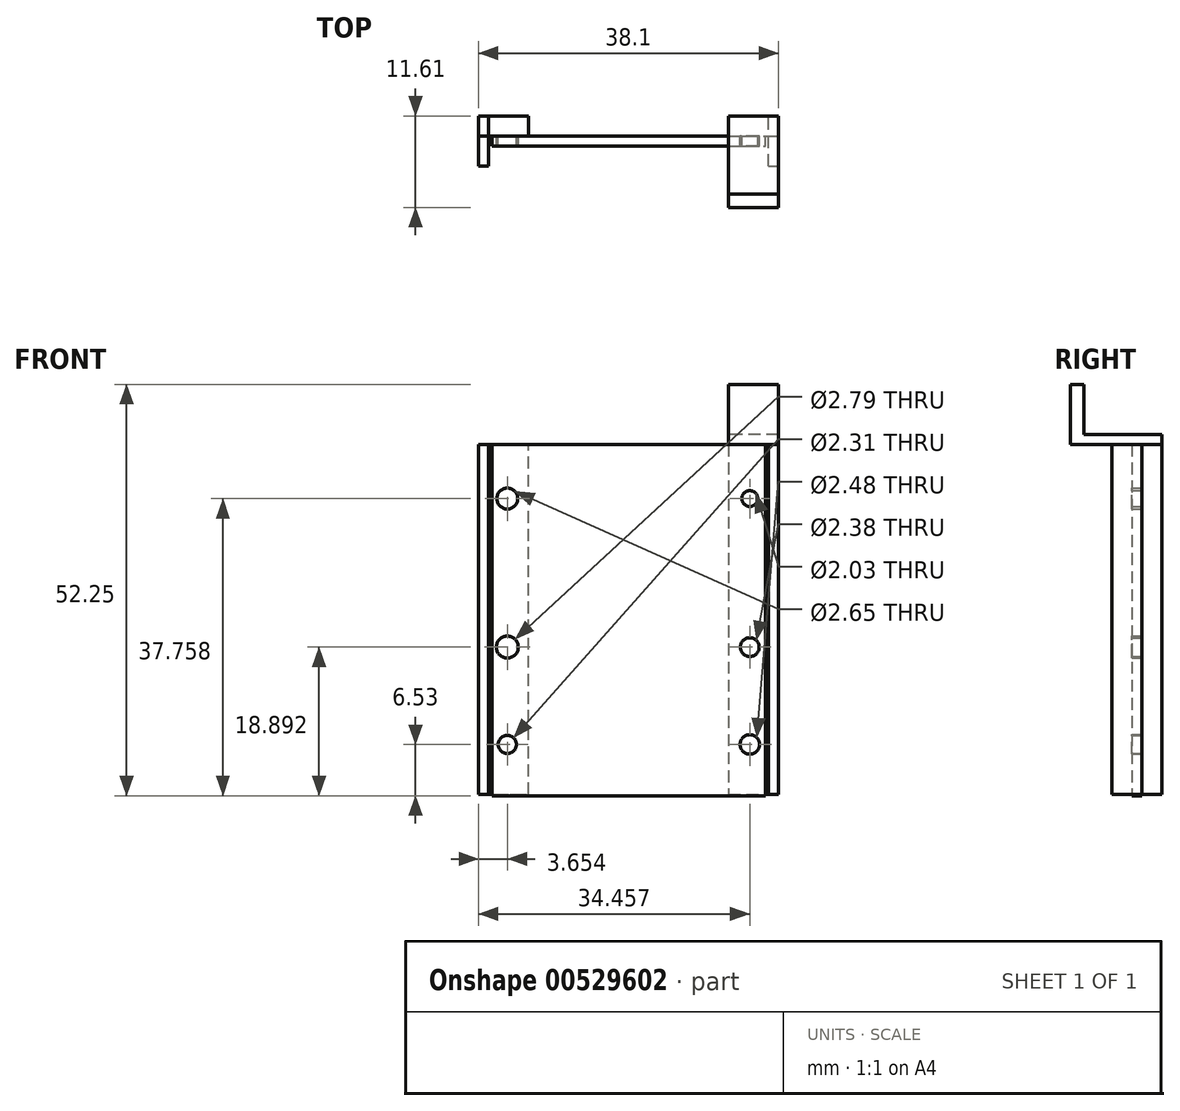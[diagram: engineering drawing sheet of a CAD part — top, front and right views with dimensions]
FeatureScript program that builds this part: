
annotation { "Feature Type Name" : "Feature", "Feature Type Description" : "" }
export const myFeature = defineFeature(function(context is Context, id is Id, definition is map)
    precondition{}
    {
        {
            var Q0;
            Q0=qCreatedBy(makeId("Front.planeOp"),FACE);
            var sketch = newSketch(context, id + "F0", { "sketchPlane" : qUnion([Q0])});
            skLineSegment(sketch, "E0.bottom", {"start": v(-19.05, -6.35) * mm, "end": v(-12.7, -6.35) * mm});
            skLineSegment(sketch, "E0.top", {"start": v(-19.05, 38.1) * mm, "end": v(-12.7, 38.1) * mm});
            skLineSegment(sketch, "E0.left", {"start": v(-19.05, -6.35) * mm, "end": v(-19.05, 38.1) * mm});
            skLineSegment(sketch, "E0.right", {"start": v(-12.7, -6.35) * mm, "end": v(-12.7, 38.1) * mm});
            skLineSegment(sketch, "E1.bottom", {"start": v(12.7, 38.1) * mm, "end": v(19.05, 38.1) * mm});
            skLineSegment(sketch, "E1.top", {"start": v(12.7, -6.35) * mm, "end": v(19.05, -6.35) * mm});
            skLineSegment(sketch, "E1.left", {"start": v(12.7, 38.1) * mm, "end": v(12.7, -6.35) * mm});
            skLineSegment(sketch, "E1.right", {"start": v(19.05, 38.1) * mm, "end": v(19.05, -6.35) * mm});
            skLineSegment(sketch, "E2", {"start": v(-17.78, -6.35) * mm, "end": v(-17.78, 38.1) * mm});
            skLineSegment(sketch, "E3", {"start": v(17.78, -6.35) * mm, "end": v(17.78, 38.1) * mm});
            skSolve(sketch);
        }
        {
            var Q0;
            {var subQ0=sQuery(id+"F0.wireOp",EDGE,"E0.left");Q0=makeQuery(id+"F0.imprint","IMPRINT",FACE,{"disambiguationData":[TD([[makeQuery(id+"F0.imprint","IMPRINT",EDGE,{"derivedFrom":subQ0}),-1.0]])]});}
            var Q1;
            {var subQ0=sQuery(id+"F0.wireOp",EDGE,"E1.right");Q1=makeQuery(id+"F0.imprint","IMPRINT",FACE,{"disambiguationData":[TD([[makeQuery(id+"F0.imprint","IMPRINT",EDGE,{"derivedFrom":subQ0}),-1.0]])]});}
            extrude(context, id + "F1", {"entities" : qUnion([Q0, Q1]), "depth" : 6.35 * mm, "offsetDistance" : 25.4 * mm});
        }
        {
            var Q0;
            Q0 = qSketchRegion(id + "F0", true);
            extrude(context, id + "F2", {"entities" : qUnion([Q0]), "depth" : 2.54 * mm, "offsetDistance" : 25.4 * mm});
        }
        {
            var Q0;
            Q0=makeQuery(id+"F2.opExtrude","CAP_FACE",FACE,{"disambiguationData":[OSD([sQuery(id+"F0.wireOp",EDGE,"E0.bottom"),sQuery(id+"F0.wireOp",EDGE,"E0.top"),sQuery(id+"F0.wireOp",EDGE,"E0.left"),sQuery(id+"F0.wireOp",EDGE,"E0.right")])],"isStart":false});
            var sketch = newSketch(context, id + "F3", { "sketchPlane" : qUnion([Q0])});
            skCircle(sketch, "E4", {"center": v(-15.4, 0) * mm, "radius": 1.15 * mm});
            skCircle(sketch, "E5", {"center": v(-15.4, 12.36) * mm, "radius": 1.4 * mm});
            skCircle(sketch, "E6", {"center": v(-15.4, 31.23) * mm, "radius": 1.33 * mm});
            skCircle(sketch, "E7", {"center": v(15.4, 0) * mm, "radius": 1.24 * mm});
            skCircle(sketch, "E8", {"center": v(15.4, 12.36) * mm, "radius": 1.2 * mm});
            skCircle(sketch, "E9", {"center": v(15.4, 31.23) * mm, "radius": 1.01 * mm});
            skLineSegment(sketch, "E10.bottom", {"start": v(-17.33, 38.1) * mm, "end": v(17.4, 38.1) * mm});
            skLineSegment(sketch, "E10.top", {"start": v(-17.33, -6.53) * mm, "end": v(17.4, -6.53) * mm});
            skLineSegment(sketch, "E10.left", {"start": v(-17.33, 38.1) * mm, "end": v(-17.33, -6.53) * mm});
            skLineSegment(sketch, "E10.right", {"start": v(17.4, 38.1) * mm, "end": v(17.4, -6.53) * mm});
            skSolve(sketch);
        }
        {
            var Q0;
            Q0 = qSketchRegion(id + "F3", true);
            extrude(context, id + "F4", {"entities" : qUnion([Q0]), "depth" : 1.27 * mm, "offsetDistance" : 25.4 * mm});
        }
        {
            var Q0;
            Q0=makeQuery(id+"F2.opExtrude","SWEPT_FACE",FACE,{"disambiguationData":[OSD([sQuery(id+"F0.wireOp",EDGE,"E1.bottom")])]});
            var sketch = newSketch(context, id + "F5", { "sketchPlane" : qUnion([Q0])});
            skLineSegment(sketch, "E11.bottom", {"start": v(19.05, 0) * mm, "end": v(12.69, 0) * mm});
            skLineSegment(sketch, "E11.top", {"start": v(19.05, -11.6) * mm, "end": v(12.69, -11.6) * mm});
            skLineSegment(sketch, "E11.left", {"start": v(19.05, 0) * mm, "end": v(19.05, -11.6) * mm});
            skLineSegment(sketch, "E11.right", {"start": v(12.69, 0) * mm, "end": v(12.69, -11.6) * mm});
            skSolve(sketch);
        }
        {
            var Q0;
            {var subQ4=sQuery(id+"F5.wireOp",EDGE,"E11.top");Q0=makeQuery(id+"F5.imprint","IMPRINT",FACE,{"disambiguationData":[TD([[makeQuery(id+"F5.imprint","IMPRINT",EDGE,{"derivedFrom":subQ4}),-1.0]])]});}
            var Q1;
            {var subQ1=sQuery(id+"F0.wireOp",EDGE,"E1.bottom");var subQ5=makeQuery(id+"F2.opExtrude","CAP_EDGE",EDGE,{"disambiguationData":[OSD([subQ1])],"isStart":false});Q1=makeQuery(id+"F5.imprint","IMPRINT",FACE,{"disambiguationData":[TD([[makeQuery(id+"F5.imprint","IMPRINT",EDGE,{"derivedFrom":subQ5}),1.0]])]});}
            extrude(context, id + "F6", {"entities" : qUnion([Q0, Q1]), "depth" : 1.27 * mm, "offsetDistance" : 25.4 * mm});
        }
        {
            var Q0;
            Q0=makeQuery(id+"F6.opExtrude","CAP_FACE",FACE,{"disambiguationData":[OSD([sQuery(id+"F5.wireOp",EDGE,"E11.bottom"),sQuery(id+"F5.wireOp",EDGE,"E11.top"),sQuery(id+"F5.wireOp",EDGE,"E11.left"),sQuery(id+"F5.wireOp",EDGE,"E11.right")])],"isStart":false});
            var sketch = newSketch(context, id + "F7", { "sketchPlane" : qUnion([Q0])});
            skLineSegment(sketch, "E12.bottom", {"start": v(19.05, -11.6) * mm, "end": v(12.69, -11.6) * mm});
            skLineSegment(sketch, "E12.top", {"start": v(19.05, -9.92) * mm, "end": v(12.69, -9.92) * mm});
            skLineSegment(sketch, "E12.left", {"start": v(19.05, -11.6) * mm, "end": v(19.05, -9.92) * mm});
            skLineSegment(sketch, "E12.right", {"start": v(12.69, -11.6) * mm, "end": v(12.69, -9.92) * mm});
            skSolve(sketch);
        }
        {
            var Q0;
            Q0=makeQuery(id+"F7.imprint","IMPRINT",FACE,{"disambiguationData":[TD([[makeQuery(id+"F7.imprint","IMPRINT",EDGE,{"derivedFrom":sQuery(id+"F7.wireOp",EDGE,"E12.bottom")}),-1.0]])]});
            extrude(context, id + "F8", {"entities" : qUnion([Q0]), "operationType" : NewBodyOperationType.ADD, "depth" : 6.35 * mm, "offsetDistance" : 25.4 * mm});
        }
    });
